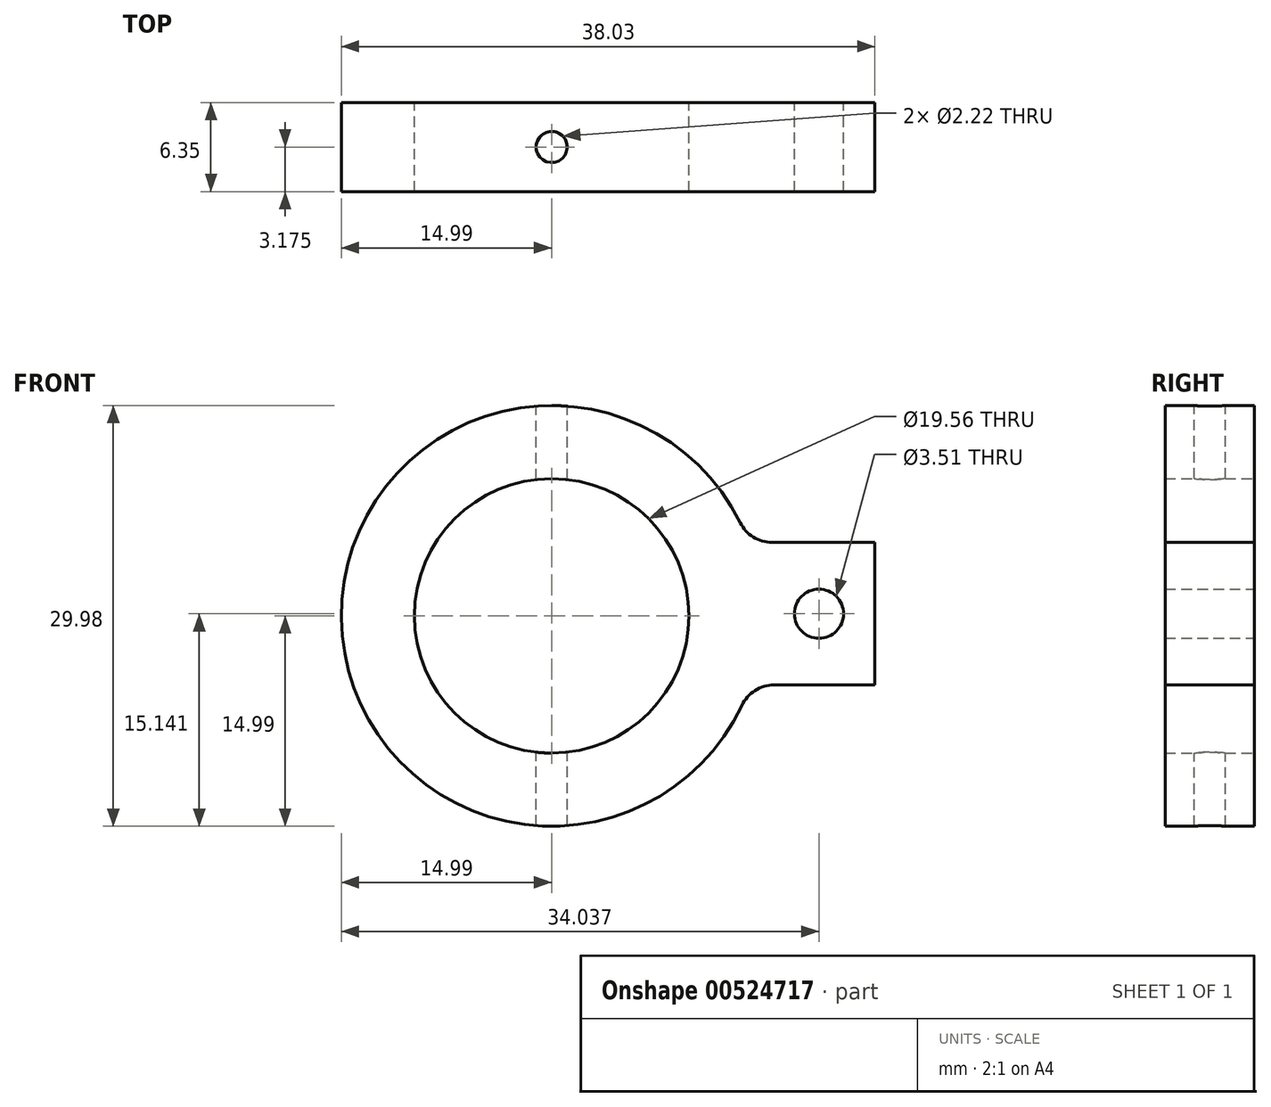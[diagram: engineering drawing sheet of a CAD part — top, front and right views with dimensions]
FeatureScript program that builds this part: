
annotation { "Feature Type Name" : "Feature", "Feature Type Description" : "" }
export const myFeature = defineFeature(function(context is Context, id is Id, definition is map)
    precondition{}
    {
        {
            var Q0;
            Q0=qCreatedBy(makeId("Front.planeOp"),FACE);
            var sketch = newSketch(context, id + "F0", { "sketchPlane" : qUnion([Q0])});
            skCircle(sketch, "E0", {"center": v(0, 0) * mm, "radius": 9.78 * mm});
            skCircle(sketch, "E1", {"center": v(0, 0) * mm, "radius": 14.99 * mm});
            skLineSegment(sketch, "E2.bottom", {"start": v(14.04, 5.23) * mm, "end": v(23.04, 5.23) * mm});
            skLineSegment(sketch, "E2.top", {"start": v(14.04, -4.93) * mm, "end": v(23.04, -4.93) * mm});
            skLineSegment(sketch, "E2.left", {"start": v(14.04, 5.23) * mm, "end": v(14.04, -4.93) * mm});
            skLineSegment(sketch, "E2.right", {"start": v(23.04, 5.23) * mm, "end": v(23.04, -4.93) * mm});
            skCircle(sketch, "E3", {"center": v(19.05, 0.15) * mm, "radius": 1.75 * mm});
            skSolve(sketch);
        }
        {
            var Q0;
            Q0 = qSketchRegion(id + "F0", true);
            extrude(context, id + "F1", {"entities" : qUnion([Q0]), "depth" : 6.35 * mm, "offsetDistance" : 25.4 * mm});
        }
        {
            var Q0;
            Q0=qCreatedBy(makeId("Top.planeOp"),FACE);
            var sketch = newSketch(context, id + "F2", { "sketchPlane" : qUnion([Q0])});
            skCircle(sketch, "E4", {"center": v(0, -3.18) * mm, "radius": 1.11 * mm});
            skSolve(sketch);
        }
        {
            var Q0;
            Q0 = qSketchRegion(id + "F2", true);
            extrude(context, id + "F3", {"entities" : qUnion([Q0]), "operationType" : NewBodyOperationType.REMOVE, "oppositeDirection" : true, "depth" : 50.8 * mm, "offsetDistance" : 25.4 * mm, "symmetric" : true});
        }
        {
            var Q0;
            Q0=makeQuery(id+"F1.opExtrude","SWEPT_EDGE",EDGE,{"disambiguationData":[OSD([sQuery(id+"F0.wireOp",EDGE,"E1"),sQuery(id+"F0.wireOp",EDGE,"E2.bottom"),sQuery(id+"F0.wireOp",EDGE,"E2.left")])]});
            fillet(context, id + "F4", {"entities" : qUnion([Q0]), "radius" : 2.54 * mm, "tangentPropagation" : true, "allowEdgeOverflow" : false});
        }
        {
            var Q0;
            Q0=makeQuery(id+"F1.opExtrude","SWEPT_EDGE",EDGE,{"disambiguationData":[OSD([sQuery(id+"F0.wireOp",EDGE,"E1"),sQuery(id+"F0.wireOp",EDGE,"E2.top")])]});
            fillet(context, id + "F5", {"entities" : qUnion([Q0]), "radius" : 2.54 * mm, "tangentPropagation" : true, "allowEdgeOverflow" : false});
        }
    });
